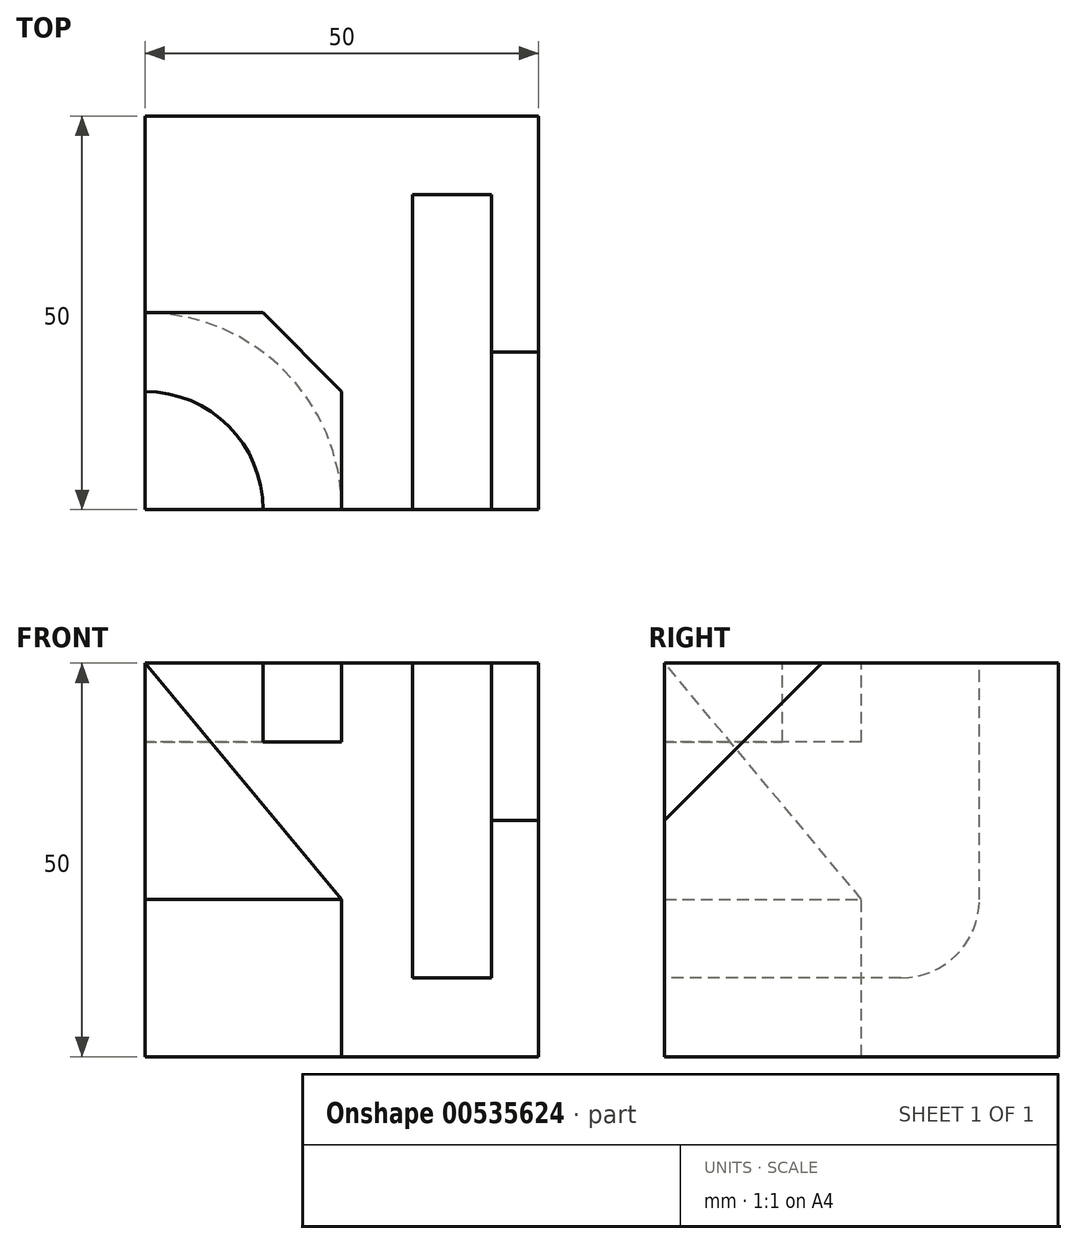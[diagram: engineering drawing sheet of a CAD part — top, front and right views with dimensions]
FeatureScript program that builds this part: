
annotation { "Feature Type Name" : "Feature", "Feature Type Description" : "" }
export const myFeature = defineFeature(function(context is Context, id is Id, definition is map)
    precondition{}
    {
        {
            var Q0;
            Q0=qCreatedBy(makeId("Top.planeOp"),FACE);
            var sketch = newSketch(context, id + "F0", { "sketchPlane" : qUnion([Q0])});
            skLineSegment(sketch, "E0.bottom", {"start": v(-31.2, 26) * mm, "end": v(18.8, 26) * mm});
            skLineSegment(sketch, "E0.top", {"start": v(-31.2, -24) * mm, "end": v(18.8, -24) * mm});
            skLineSegment(sketch, "E0.left", {"start": v(-31.2, 26) * mm, "end": v(-31.2, -24) * mm});
            skLineSegment(sketch, "E0.right", {"start": v(18.8, 26) * mm, "end": v(18.8, -24) * mm});
            skSolve(sketch);
        }
        {
            var Q0;
            Q0 = qSketchRegion(id + "F0", true);
            extrude(context, id + "F1", {"entities" : qUnion([Q0]), "depth" : 50 * mm, "offsetDistance" : 25 * mm});
        }
        {
            var Q0;
            Q0=makeQuery(id+"F1.opExtrude","CAP_FACE",FACE,{"disambiguationData":[OSD([sQuery(id+"F0.wireOp",EDGE,"E0.bottom"),sQuery(id+"F0.wireOp",EDGE,"E0.top"),sQuery(id+"F0.wireOp",EDGE,"E0.left"),sQuery(id+"F0.wireOp",EDGE,"E0.right")])],"isStart":false});
            var sketch = newSketch(context, id + "F2", { "sketchPlane" : qUnion([Q0])});
            skLineSegment(sketch, "E1.bottom", {"start": v(-31.2, 1) * mm, "end": v(-6.2, 1) * mm});
            skLineSegment(sketch, "E1.top", {"start": v(-31.2, -24) * mm, "end": v(-6.2, -24) * mm});
            skLineSegment(sketch, "E1.left", {"start": v(-31.2, 1) * mm, "end": v(-31.2, -24) * mm});
            skLineSegment(sketch, "E1.right", {"start": v(-6.2, 1) * mm, "end": v(-6.2, -24) * mm});
            skSolve(sketch);
        }
        {
            var Q0;
            Q0=makeQuery(id+"F2.imprint","IMPRINT",FACE,{"disambiguationData":[TD([[makeQuery(id+"F2.imprint","IMPRINT",EDGE,{"derivedFrom":sQuery(id+"F2.wireOp",EDGE,"E1.bottom")}),-1.0]])]});
            var sketch = newSketch(context, id + "F3", { "sketchPlane" : qUnion([Q0])});
            skCircle(sketch, "E2", {"center": v(-31.2, -24) * mm, "radius": 15 * mm});
            skSolve(sketch);
        }
        {
            var Q0;
            {var subQ4=makeQuery(id+"F2.imprint","IMPRINT",EDGE,{"derivedFrom":sQuery(id+"F2.wireOp",EDGE,"E1.bottom")});Q0=makeQuery(id+"F3.imprint","IMPRINT",FACE,{"disambiguationData":[TD([[makeQuery(id+"F3.imprint","IMPRINT",EDGE,{"derivedFrom":subQ4}),-1.0]])]});}
            extrude(context, id + "F4", {"entities" : qUnion([Q0]), "operationType" : NewBodyOperationType.REMOVE, "oppositeDirection" : true, "depth" : 10 * mm, "offsetDistance" : 25 * mm});
        }
        {
            var Q0;
            Q0=makeQuery(id+"F4.boolean.opBoolean","COPY",EDGE,{"derivedFrom":makeQuery(id+"F4.opExtrude","SWEPT_EDGE",EDGE,{"disambiguationData":[OSD([sQuery(id+"F2.wireOp",EDGE,"E1.bottom"),sQuery(id+"F2.wireOp",EDGE,"E1.right")])]})});
            chamfer(context, id + "F5", {"entities" : qUnion([Q0]), "width" : 10 * mm, "tangentPropagation" : true});
        }
        {
            var Q0;
            {var subQ4=sQuery(id+"F2.wireOp",EDGE,"E1.bottom");Q0=makeQuery(id+"F2.imprint","IMPRINT",FACE,{"disambiguationData":[TD([[makeQuery(id+"F2.imprint","IMPRINT",EDGE,{"derivedFrom":subQ4}),1.0]])]});}
            var sketch = newSketch(context, id + "F6", { "sketchPlane" : qUnion([Q0])});
            skLineSegment(sketch, "E3.bottom", {"start": v(2.8, 16) * mm, "end": v(12.8, 16) * mm});
            skLineSegment(sketch, "E3.top", {"start": v(2.8, -24) * mm, "end": v(12.8, -24) * mm});
            skLineSegment(sketch, "E3.left", {"start": v(2.8, 16) * mm, "end": v(2.8, -24) * mm});
            skLineSegment(sketch, "E3.right", {"start": v(12.8, 16) * mm, "end": v(12.8, -24) * mm});
            skSolve(sketch);
        }
        {
            var Q0;
            Q0=makeQuery(id+"F1.opExtrude","CAP_FACE",FACE,{"disambiguationData":[OSD([sQuery(id+"F0.wireOp",EDGE,"E0.bottom"),sQuery(id+"F0.wireOp",EDGE,"E0.top"),sQuery(id+"F0.wireOp",EDGE,"E0.left"),sQuery(id+"F0.wireOp",EDGE,"E0.right")])],"isStart":true});
            cPlane(context, id + "F7", {"entities" : qUnion([Q0]), "cplaneType" : CPlaneType.OFFSET, "offset" : 10 * mm, "oppositeDirection" : true, "width" : 150 * mm, "height" : 150 * mm});
        }
        {
            var Q0;
            Q0 = qSketchRegion(id + "F6", true);
            var Q1;
            Q1=qCreatedBy(id+"F7.planeOp",FACE);
            extrude(context, id + "F8", {"entities" : qUnion([Q0]), "operationType" : NewBodyOperationType.REMOVE, "endBound" : BoundingType.UP_TO_SURFACE, "oppositeDirection" : true, "depth" : 25 * mm, "endBoundEntityFace" : qUnion([Q1]), "offsetDistance" : 25 * mm});
        }
        {
            var Q0;
            Q0=makeQuery(id+"F8.boolean.opBoolean","COPY",EDGE,{"derivedFrom":makeQuery(id+"F8.opExtrude","CAP_EDGE",EDGE,{"disambiguationData":[OSD([sQuery(id+"F6.wireOp",EDGE,"E3.bottom")])],"isStart":false})});
            fillet(context, id + "F9", {"entities" : qUnion([Q0]), "radius" : 10 * mm, "tangentPropagation" : true, "allowEdgeOverflow" : false});
        }
        {
            var Q0;
            Q0=makeQuery(id+"F1.opExtrude","SWEPT_FACE",FACE,{"disambiguationData":[OSD([sQuery(id+"F0.wireOp",EDGE,"E0.right")])]});
            var sketch = newSketch(context, id + "F10", { "sketchPlane" : qUnion([Q0])});
            skLineSegment(sketch, "E4", {"start": v(-24, 50) * mm, "end": v(-4, 50) * mm});
            skLineSegment(sketch, "E5", {"start": v(-4, 50) * mm, "end": v(-24, 30) * mm});
            skLineSegment(sketch, "E6", {"start": v(-24, 30) * mm, "end": v(-24, 50) * mm});
            skSolve(sketch);
        }
        {
            var Q0;
            Q0 = qSketchRegion(id + "F10", true);
            extrude(context, id + "F11", {"entities" : qUnion([Q0]), "operationType" : NewBodyOperationType.REMOVE, "oppositeDirection" : true, "depth" : 6 * mm, "offsetDistance" : 25 * mm});
        }
        {
            var Q0;
            Q0=makeQuery(id+"F1.opExtrude","SWEPT_FACE",FACE,{"disambiguationData":[OSD([sQuery(id+"F0.wireOp",EDGE,"E0.top")])]});
            var sketch = newSketch(context, id + "F12", { "sketchPlane" : qUnion([Q0])});
            skLineSegment(sketch, "E7", {"start": v(-31.2, 50) * mm, "end": v(-6.2, 20) * mm});
            skLineSegment(sketch, "E8", {"start": v(-6.2, 20) * mm, "end": v(-6.2, 0) * mm});
            skLineSegment(sketch, "E9", {"start": v(-6.2, 0) * mm, "end": v(-31.2, 0) * mm});
            skLineSegment(sketch, "E10", {"start": v(-31.2, 0) * mm, "end": v(-31.2, 50) * mm});
            skSolve(sketch);
        }
        {
            var Q0;
            Q0=makeQuery(id+"F12.imprint","IMPRINT",FACE,{"disambiguationData":[TD([[makeQuery(id+"F12.imprint","IMPRINT",EDGE,{"derivedFrom":sQuery(id+"F12.wireOp",EDGE,"E7")}),-1.0]])]});
            var Q1;
            Q1=sQuery(id+"F12.wireOp",EDGE,"E10");
            revolve(context, id + "F13", {"operationType" : NewBodyOperationType.REMOVE, "entities" : qUnion([Q0]), "axis" : qUnion([Q1]), "revolveType" : RevolveType.FULL, "oppositeDirection" : true});
        }
    });
